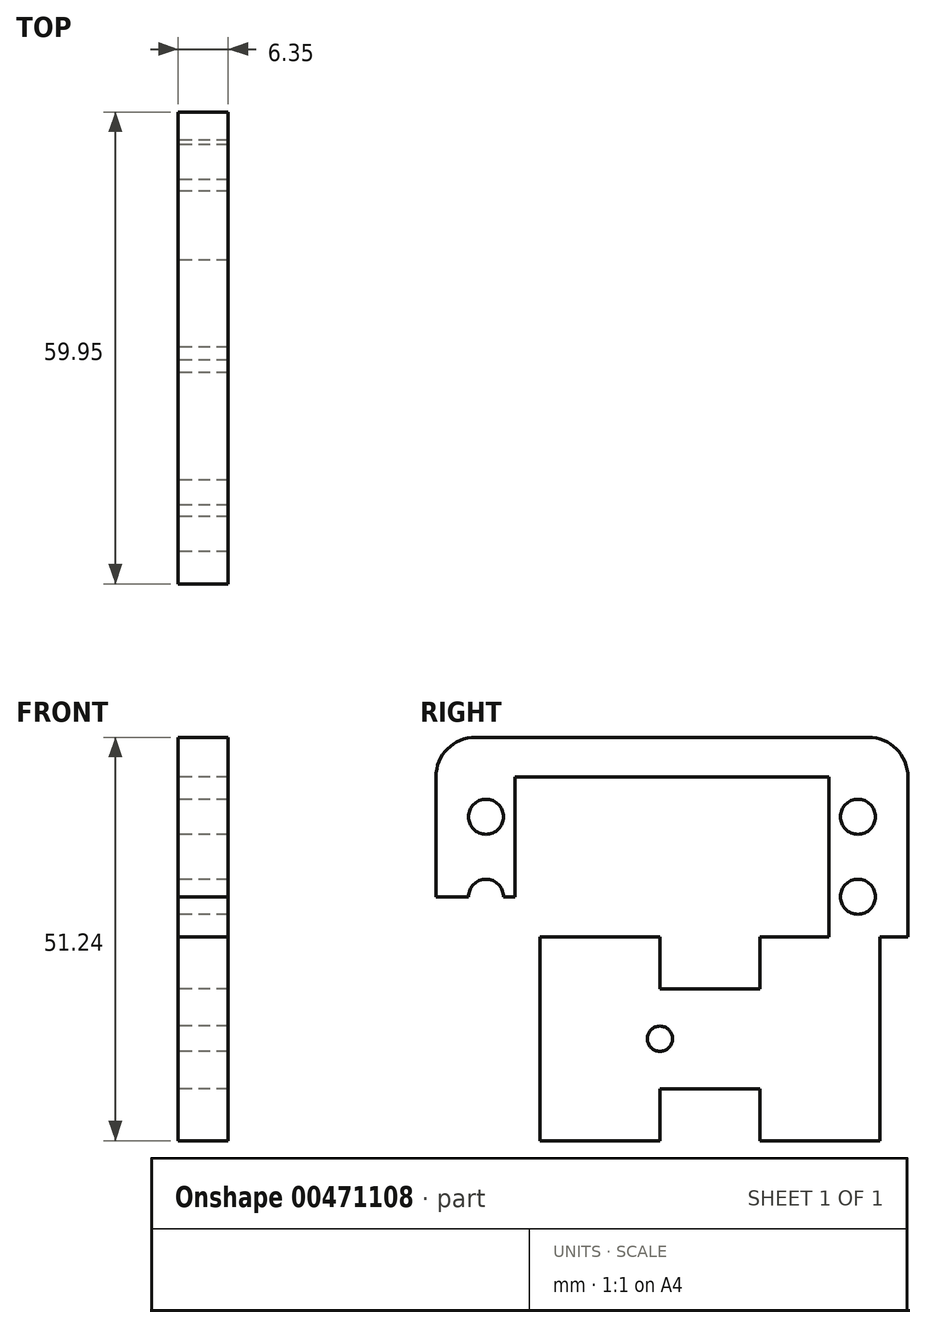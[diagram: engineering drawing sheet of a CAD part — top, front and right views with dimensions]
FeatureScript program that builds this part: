
annotation { "Feature Type Name" : "Feature", "Feature Type Description" : "" }
export const myFeature = defineFeature(function(context is Context, id is Id, definition is map)
    precondition{}
    {
        {
            var Q0;
            Q0=qCreatedBy(makeId("Right.planeOp"),FACE);
            var sketch = newSketch(context, id + "F0", { "sketchPlane" : qUnion([Q0])});
            skLineSegment(sketch, "E0", {"start": v(-6.35, 0) * mm, "end": v(-6.35, 6.6) * mm});
            skLineSegment(sketch, "E1", {"start": v(-6.35, 6.6) * mm, "end": v(-21.59, 6.6) * mm});
            skLineSegment(sketch, "E2", {"start": v(0, 0) * mm, "end": v(0, 21.05) * mm, "construction": true});
            skLineSegment(sketch, "E3.MirrorCS", {"start": v(6.35, 0) * mm, "end": v(6.35, 6.6) * mm});
            skLineSegment(sketch, "E4.MirrorCS", {"start": v(6.35, 6.6) * mm, "end": v(15.11, 6.6) * mm});
            skLineSegment(sketch, "E5", {"start": v(-6.35, 0) * mm, "end": v(6.35, 0) * mm});
            skLineSegment(sketch, "E6", {"start": v(-21.59, 6.6) * mm, "end": v(-21.59, -19.3) * mm});
            skPoint(sketch, "E7.endSnap0", {"position": v(-21.59, -6.35) * mm});
            skLineSegment(sketch, "E8.MirrorCS", {"start": v(-6.35, -19.3) * mm, "end": v(-21.59, -19.3) * mm});
            skLineSegment(sketch, "E9.MirrorCS", {"start": v(-6.35, -12.7) * mm, "end": v(-6.35, -19.3) * mm});
            skLineSegment(sketch, "E10.MirrorCS", {"start": v(-6.35, -12.7) * mm, "end": v(6.35, -12.7) * mm});
            skLineSegment(sketch, "E11.MirrorCS", {"start": v(6.35, -12.7) * mm, "end": v(6.35, -19.3) * mm});
            skLineSegment(sketch, "E12.MirrorCS", {"start": v(6.35, -19.3) * mm, "end": v(21.59, -19.3) * mm});
            skCircle(sketch, "E13", {"center": v(18.8, 11.68) * mm, "radius": 2.22 * mm});
            skLineSegment(sketch, "E14", {"start": v(18.8, 11.68) * mm, "end": v(18.8, 16.76) * mm, "construction": true});
            skLineSegment(sketch, "E15", {"start": v(18.8, 16.76) * mm, "end": v(21.59, 16.76) * mm, "construction": true});
            skCircle(sketch, "E16.MirrorC", {"center": v(18.8, 21.84) * mm, "radius": 2.22 * mm});
            skLineSegment(sketch, "E17", {"start": v(18.8, 21.84) * mm, "end": v(-4.83, 21.84) * mm, "construction": true});
            skLineSegment(sketch, "E18", {"start": v(-4.83, 21.84) * mm, "end": v(-4.83, 16.1) * mm, "construction": true});
            skCircle(sketch, "E19.MirrorC", {"center": v(-28.45, 21.84) * mm, "radius": 2.22 * mm});
            skArc(sketch, "E20.MirrorC", {"start": v(-30.67, 11.68) * mm, "mid": v(-28.45, 13.9) * mm, "end": v(-26.23, 11.68) * mm});
            skLineSegment(sketch, "E21", {"start": v(-34.8, 26.92) * mm, "end": v(-34.8, 11.68) * mm});
            skLineSegment(sketch, "E22", {"start": v(-24.77, 11.68) * mm, "end": v(-24.77, 26.92) * mm});
            skLineSegment(sketch, "E23.MirrorCS", {"start": v(15.11, 6.6) * mm, "end": v(15.11, 26.92) * mm});
            skLineSegment(sketch, "E24.MirrorCS", {"start": v(25.15, 26.92) * mm, "end": v(25.15, 6.6) * mm});
            skLineSegment(sketch, "E25", {"start": v(21.59, -19.3) * mm, "end": v(21.59, 6.6) * mm});
            skArc(sketch, "E26", {"start": v(-29.78, 31.94) * mm, "mid": v(-33.33, 30.47) * mm, "end": v(-34.8, 26.92) * mm});
            skArc(sketch, "E27.MirrorCS", {"start": v(20.13, 31.94) * mm, "mid": v(23.68, 30.47) * mm, "end": v(25.15, 26.92) * mm});
            skLineSegment(sketch, "E28", {"start": v(-29.78, 31.94) * mm, "end": v(20.13, 31.94) * mm});
            skPoint(sketch, "E29.orphan", {"position": v(15.11, 26.92) * mm});
            skLineSegment(sketch, "E30", {"start": v(-24.77, 26.92) * mm, "end": v(15.11, 26.92) * mm});
            skLineSegment(sketch, "E31", {"start": v(25.15, 6.6) * mm, "end": v(21.59, 6.6) * mm});
            skLineSegment(sketch, "E32", {"start": v(-34.8, 11.68) * mm, "end": v(-30.67, 11.68) * mm});
            skPoint(sketch, "E32.startSnap0", {"position": v(-34.8, 16.76) * mm});
            skLineSegment(sketch, "E33.trimOffspring", {"start": v(-26.23, 11.68) * mm, "end": v(-24.77, 11.68) * mm});
            skCircle(sketch, "E34", {"center": v(-6.35, -6.35) * mm, "radius": 1.6 * mm});
            skSolve(sketch);
        }
        {
            var Q0;
            Q0=makeQuery(id+"F0.imprint","IMPRINT",FACE,{"disambiguationData":[TD([[makeQuery(id+"F0.imprint","IMPRINT",EDGE,{"derivedFrom":sQuery(id+"F0.wireOp",EDGE,"E0")}),1.0]])]});
            extrude(context, id + "F1", {"entities" : qUnion([Q0]), "depth" : 6.35 * mm});
        }
    });
